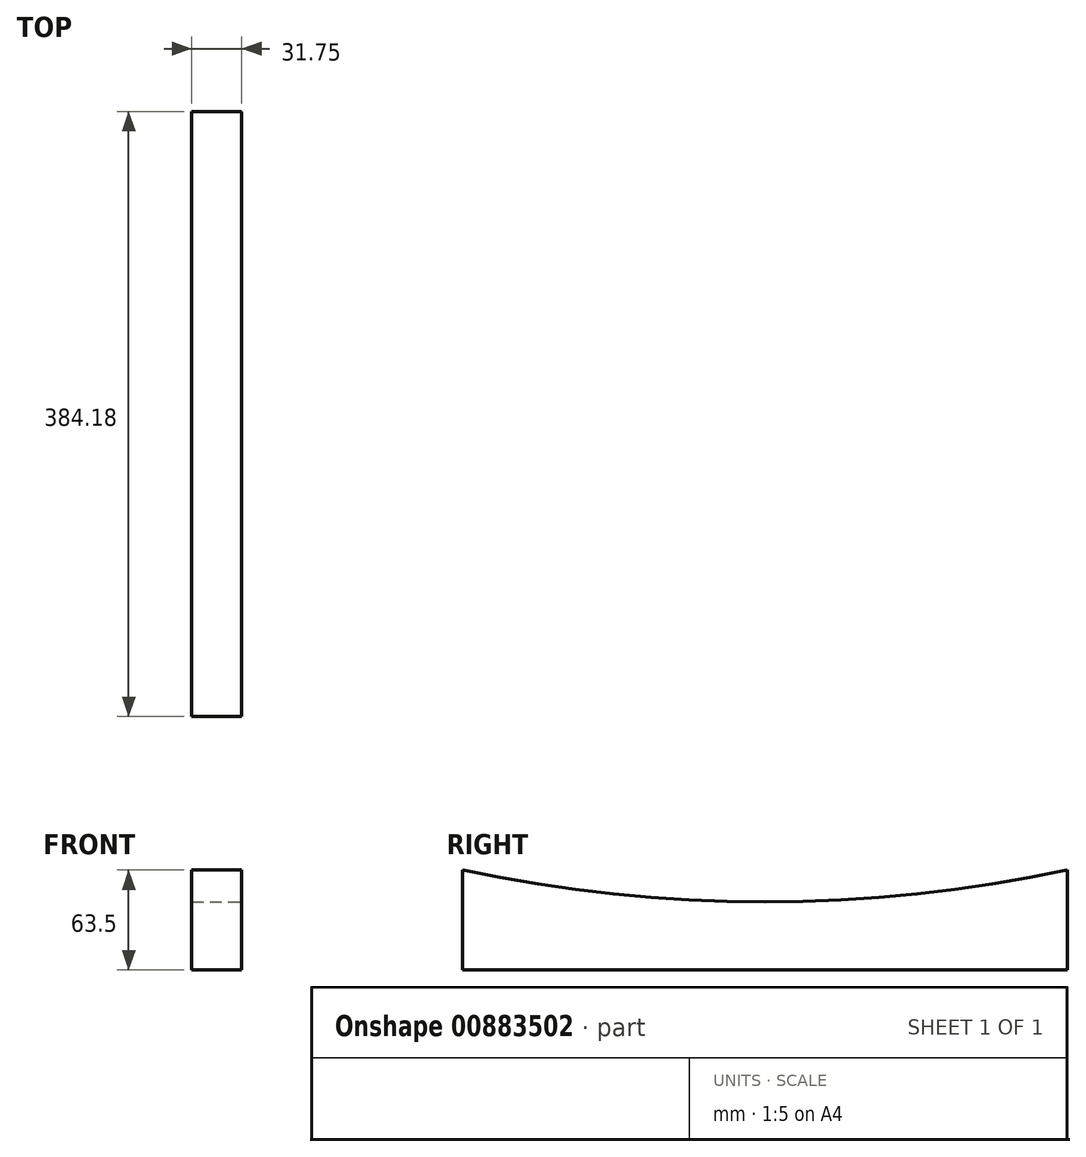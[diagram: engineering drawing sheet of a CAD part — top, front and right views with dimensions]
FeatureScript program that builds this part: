
annotation { "Feature Type Name" : "Feature", "Feature Type Description" : "" }
export const myFeature = defineFeature(function(context is Context, id is Id, definition is map)
    precondition{}
    {
        {
            var Q0;
            Q0=qCreatedBy(makeId("Front.planeOp"),FACE);
            var sketch = newSketch(context, id + "F0", { "sketchPlane" : qUnion([Q0])});
            skLineSegment(sketch, "E0.bottom", {"start": v(0, 0) * mm, "end": v(31.75, 0) * mm});
            skLineSegment(sketch, "E0.top", {"start": v(0, 63.5) * mm, "end": v(31.75, 63.5) * mm});
            skLineSegment(sketch, "E0.left", {"start": v(0, 0) * mm, "end": v(0, 63.5) * mm});
            skLineSegment(sketch, "E0.right", {"start": v(31.75, 0) * mm, "end": v(31.75, 63.5) * mm});
            skSolve(sketch);
        }
        {
            var Q0;
            Q0 = qSketchRegion(id + "F0", true);
            extrude(context, id + "F1", {"entities" : qUnion([Q0]), "depth" : 384.17 * mm, "offsetDistance" : 25.4 * mm});
        }
        {
            var Q0;
            Q0=makeQuery(id+"F1.opExtrude","SWEPT_FACE",FACE,{"disambiguationData":[OSD([sQuery(id+"F0.wireOp",EDGE,"E0.right")])]});
            var sketch = newSketch(context, id + "F2", { "sketchPlane" : qUnion([Q0])});
            skCircle(sketch, "E1", {"center": v(-192.09, 957.5) * mm, "radius": 914.4 * mm});
            skSolve(sketch);
        }
        {
            var Q0;
            {var subQ1=sQuery(id+"F0.wireOp",EDGE,"E0.right");var subQ2=makeQuery(id+"F1.opExtrude","SWEPT_EDGE",EDGE,{"disambiguationData":[OSD([sQuery(id+"F0.wireOp",EDGE,"E0.top"),subQ1])]});Q0=makeQuery(id+"F2.imprint","IMPRINT",FACE,{"disambiguationData":[TD([[makeQuery(id+"F2.imprint","IMPRINT",EDGE,{"derivedFrom":subQ2}),-1.0]])]});}
            extrude(context, id + "F3", {"entities" : qUnion([Q0]), "operationType" : NewBodyOperationType.REMOVE, "endBound" : BoundingType.UP_TO_NEXT, "oppositeDirection" : true, "depth" : 25.4 * mm, "offsetDistance" : 25.4 * mm});
        }
    });
